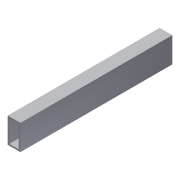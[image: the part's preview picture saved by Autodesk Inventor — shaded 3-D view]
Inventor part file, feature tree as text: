
AUTODESK INVENTOR PART (.ipt)
format: ipt  version: 2013 (Build 170138000, 138)  size: 74,752 bytes
history: native  units: in
note: dims shown in document units (in); Inventor stores cm internally (conversion verified against a paired STEP export)
features: extrude x1, sketch x1
ambient origin geometry x8: Origin, YZ Plane, XZ Plane, XY Plane, X Axis, Y Axis, Z Axis, Center Point
bodies: Solid1 (feature_tree)
feature tree (2):
  extrude  "Extrusion1"  [1 undecoded]
  sketch  "Sketch1"  dims[d5=0.0in]
note: 1 required parameter value undecoded (feature->parameter linkage not recoverable at this tier; creation-order binding heuristic only, values carry confidence <= 0.55)
